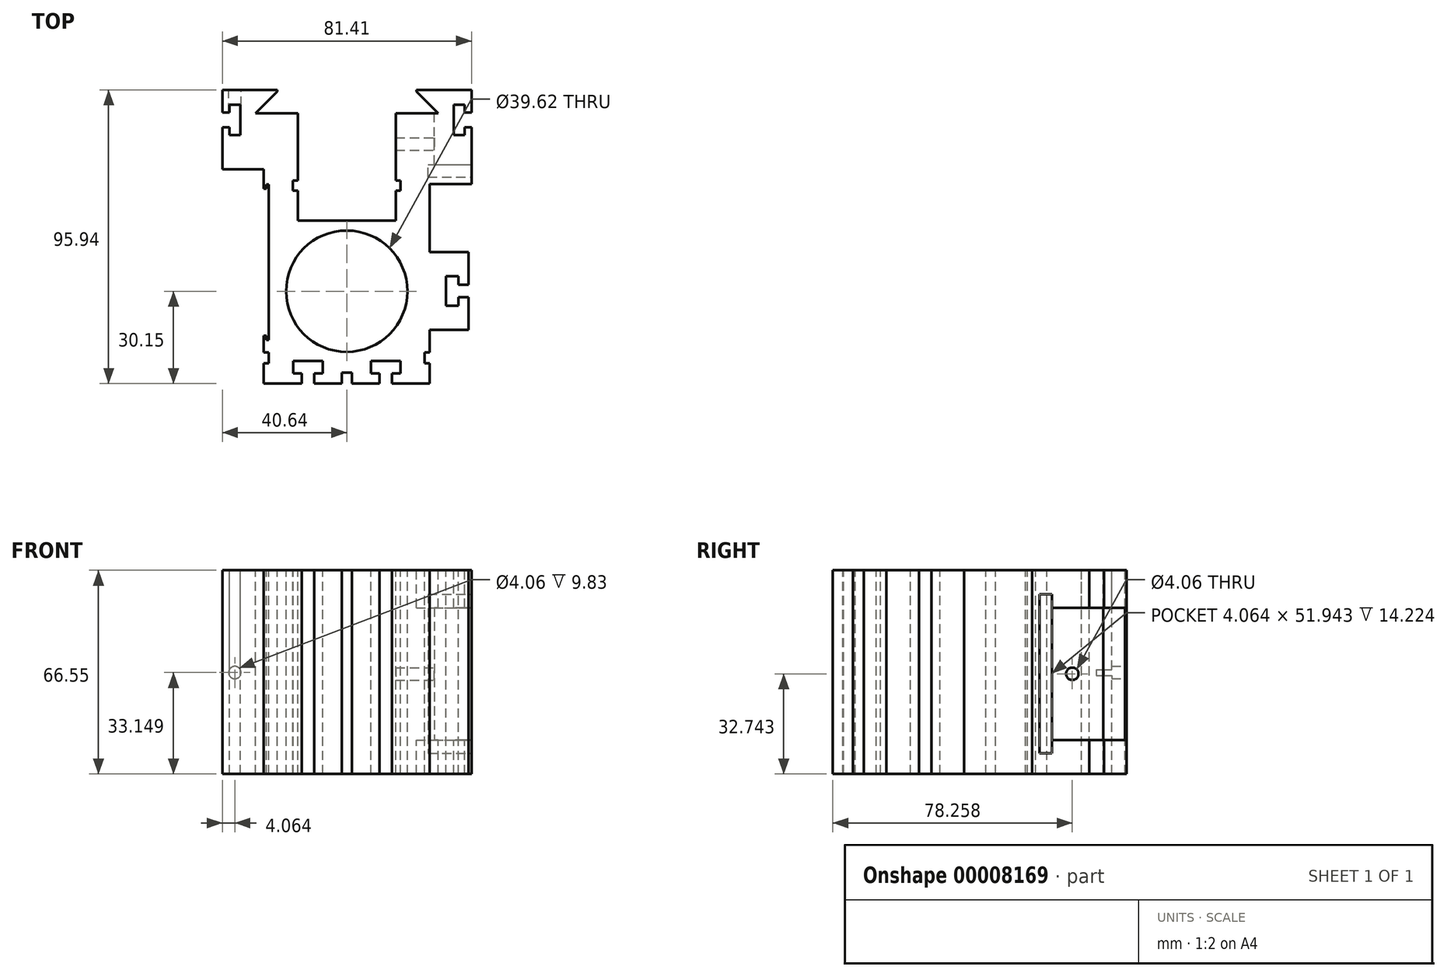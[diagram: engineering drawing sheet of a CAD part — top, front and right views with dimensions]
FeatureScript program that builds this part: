
annotation { "Feature Type Name" : "Feature", "Feature Type Description" : "" }
export const myFeature = defineFeature(function(context is Context, id is Id, definition is map)
    precondition{}
    {
        {
            var Q0;
            Q0=qCreatedBy(makeId("Top.planeOp"),FACE);
            var sketch = newSketch(context, id + "F0", { "sketchPlane" : qUnion([Q0])});
            skFitSpline(sketch, "E0.0.0", {"points": [v(-16, 23.06) * mm, v(-16, 32.87) * mm]});
            skFitSpline(sketch, "E0.0.1", {"points": [v(-16, 32.87) * mm, v(-17.6, 32.87) * mm]});
            skFitSpline(sketch, "E0.0.2", {"points": [v(-17.6, 32.87) * mm, v(-17.6, 36.17) * mm]});
            skFitSpline(sketch, "E0.0.3", {"points": [v(-17.6, 36.17) * mm, v(-16, 36.17) * mm]});
            skFitSpline(sketch, "E0.0.4", {"points": [v(-16, 36.17) * mm, v(-16, 58.17) * mm]});
            skFitSpline(sketch, "E0.0.5", {"points": [v(-16, 58.17) * mm, v(-29.84, 58.17) * mm]});
            skFitSpline(sketch, "E0.0.6", {"points": [v(-29.84, 58.17) * mm, v(-22.73, 65.28) * mm]});
            skFitSpline(sketch, "E0.0.7", {"points": [v(-22.73, 65.28) * mm, v(-22.73, 65.79) * mm]});
            skFitSpline(sketch, "E0.0.8", {"points": [v(-22.73, 65.79) * mm, v(-40.64, 65.79) * mm]});
            skFitSpline(sketch, "E0.0.9", {"points": [v(-40.64, 65.79) * mm, v(-40.64, 58.42) * mm]});
            skFitSpline(sketch, "E0.0.10", {"points": [v(-40.64, 58.42) * mm, v(-38.35, 58.42) * mm]});
            skFitSpline(sketch, "E0.0.11", {"points": [v(-38.35, 58.42) * mm, v(-38.35, 60.96) * mm]});
            skFitSpline(sketch, "E0.0.12", {"points": [v(-38.35, 60.96) * mm, v(-34.8, 60.96) * mm]});
            skFitSpline(sketch, "E0.0.13", {"points": [v(-34.8, 60.96) * mm, v(-34.8, 51.05) * mm]});
            skFitSpline(sketch, "E0.0.14", {"points": [v(-34.8, 51.05) * mm, v(-38.35, 51.05) * mm]});
            skFitSpline(sketch, "E0.0.15", {"points": [v(-38.35, 51.05) * mm, v(-38.35, 53.6) * mm]});
            skFitSpline(sketch, "E0.0.16", {"points": [v(-38.35, 53.6) * mm, v(-40.64, 53.6) * mm]});
            skFitSpline(sketch, "E0.0.17", {"points": [v(-40.64, 53.6) * mm, v(-40.64, 39.83) * mm]});
            skFitSpline(sketch, "E0.0.18", {"points": [v(-40.64, 39.83) * mm, v(-27.1, 39.83) * mm]});
            skFitSpline(sketch, "E0.0.19", {"points": [v(-27.1, 39.83) * mm, v(-27.1, 33.48) * mm]});
            skFitSpline(sketch, "E0.0.20", {"points": [v(-27.1, 33.48) * mm, v(-26.24, 33.48) * mm]});
            skFitSpline(sketch, "E0.0.21", {"points": [v(-26.24, 33.48) * mm, v(-26.24, 34.93) * mm]});
            skFitSpline(sketch, "E0.0.22", {"points": [v(-26.24, 34.93) * mm, v(-25.45, 34.93) * mm]});
            skFitSpline(sketch, "E0.0.23", {"points": [v(-25.45, 34.93) * mm, v(-25.45, -15.98) * mm]});
            skFitSpline(sketch, "E0.0.24", {"points": [v(-25.45, -15.98) * mm, v(-26.24, -15.98) * mm]});
            skFitSpline(sketch, "E0.0.25", {"points": [v(-26.24, -15.98) * mm, v(-26.24, -14.53) * mm]});
            skFitSpline(sketch, "E0.0.26", {"points": [v(-26.24, -14.53) * mm, v(-27.1, -14.53) * mm]});
            skFitSpline(sketch, "E0.0.27", {"points": [v(-27.1, -14.53) * mm, v(-27.1, -19.99) * mm]});
            skFitSpline(sketch, "E0.0.28", {"points": [v(-27.1, -19.99) * mm, v(-25.45, -19.99) * mm]});
            skFitSpline(sketch, "E0.0.29", {"points": [v(-25.45, -19.99) * mm, v(-25.45, -23.55) * mm]});
            skFitSpline(sketch, "E0.0.30", {"points": [v(-25.45, -23.55) * mm, v(-27.1, -23.55) * mm]});
            skFitSpline(sketch, "E0.0.31", {"points": [v(-27.1, -23.55) * mm, v(-27.1, -30.15) * mm]});
            skFitSpline(sketch, "E0.0.32", {"points": [v(-27.1, -30.15) * mm, v(-14.73, -30.15) * mm]});
            skFitSpline(sketch, "E0.0.33", {"points": [v(-14.73, -30.15) * mm, v(-14.73, -26.85) * mm]});
            skFitSpline(sketch, "E0.0.34", {"points": [v(-14.73, -26.85) * mm, v(-17.53, -26.85) * mm]});
            skFitSpline(sketch, "E0.0.35", {"points": [v(-17.53, -26.85) * mm, v(-17.53, -22.78) * mm]});
            skFitSpline(sketch, "E0.0.36", {"points": [v(-17.53, -22.78) * mm, v(-7.87, -22.78) * mm]});
            skFitSpline(sketch, "E0.0.37", {"points": [v(-7.87, -22.78) * mm, v(-7.87, -26.85) * mm]});
            skFitSpline(sketch, "E0.0.38", {"points": [v(-7.87, -26.85) * mm, v(-10.67, -26.85) * mm]});
            skFitSpline(sketch, "E0.0.39", {"points": [v(-10.67, -26.85) * mm, v(-10.67, -30.15) * mm]});
            skFitSpline(sketch, "E0.0.40", {"points": [v(-10.67, -30.15) * mm, v(-1.65, -30.15) * mm]});
            skFitSpline(sketch, "E0.0.41", {"points": [v(-1.65, -30.15) * mm, v(-1.65, -26.6) * mm]});
            skFitSpline(sketch, "E0.0.42", {"points": [v(-1.65, -26.6) * mm, v(1.65, -26.6) * mm]});
            skFitSpline(sketch, "E0.0.43", {"points": [v(1.65, -26.6) * mm, v(1.65, -30.15) * mm]});
            skFitSpline(sketch, "E0.0.44", {"points": [v(1.65, -30.15) * mm, v(10.67, -30.15) * mm]});
            skFitSpline(sketch, "E0.0.45", {"points": [v(10.67, -30.15) * mm, v(10.67, -26.85) * mm]});
            skFitSpline(sketch, "E0.0.46", {"points": [v(10.67, -26.85) * mm, v(7.87, -26.85) * mm]});
            skFitSpline(sketch, "E0.0.47", {"points": [v(7.87, -26.85) * mm, v(7.87, -22.78) * mm]});
            skFitSpline(sketch, "E0.0.48", {"points": [v(7.87, -22.78) * mm, v(17.53, -22.78) * mm]});
            skFitSpline(sketch, "E0.0.49", {"points": [v(17.53, -22.78) * mm, v(17.53, -26.85) * mm]});
            skFitSpline(sketch, "E0.0.50", {"points": [v(17.53, -26.85) * mm, v(14.73, -26.85) * mm]});
            skFitSpline(sketch, "E0.0.51", {"points": [v(14.73, -26.85) * mm, v(14.73, -30.15) * mm]});
            skFitSpline(sketch, "E0.0.52", {"points": [v(14.73, -30.15) * mm, v(27.1, -30.15) * mm]});
            skFitSpline(sketch, "E0.0.53", {"points": [v(27.1, -30.15) * mm, v(27.1, -23.55) * mm]});
            skFitSpline(sketch, "E0.0.54", {"points": [v(27.1, -23.55) * mm, v(25.45, -23.55) * mm]});
            skFitSpline(sketch, "E0.0.55", {"points": [v(25.45, -23.55) * mm, v(25.45, -19.99) * mm]});
            skFitSpline(sketch, "E0.0.56", {"points": [v(25.45, -19.99) * mm, v(27.1, -19.99) * mm]});
            skFitSpline(sketch, "E0.0.57", {"points": [v(27.1, -19.99) * mm, v(27.1, -12.62) * mm]});
            skFitSpline(sketch, "E0.0.58", {"points": [v(27.1, -12.62) * mm, v(39.8, -12.62) * mm]});
            skFitSpline(sketch, "E0.0.59", {"points": [v(39.8, -12.62) * mm, v(39.8, -1.96) * mm]});
            skFitSpline(sketch, "E0.0.60", {"points": [v(39.8, -1.96) * mm, v(36.5, -1.96) * mm]});
            skFitSpline(sketch, "E0.0.61", {"points": [v(36.5, -1.96) * mm, v(36.5, -4.75) * mm]});
            skFitSpline(sketch, "E0.0.62", {"points": [v(36.5, -4.75) * mm, v(32.44, -4.75) * mm]});
            skFitSpline(sketch, "E0.0.63", {"points": [v(32.44, -4.75) * mm, v(32.44, 4.9) * mm]});
            skFitSpline(sketch, "E0.0.64", {"points": [v(32.44, 4.9) * mm, v(36.5, 4.9) * mm]});
            skFitSpline(sketch, "E0.0.65", {"points": [v(36.5, 4.9) * mm, v(36.5, 2.1) * mm]});
            skFitSpline(sketch, "E0.0.66", {"points": [v(36.5, 2.1) * mm, v(39.8, 2.1) * mm]});
            skFitSpline(sketch, "E0.0.67", {"points": [v(39.8, 2.1) * mm, v(39.8, 12.78) * mm]});
            skFitSpline(sketch, "E0.0.68", {"points": [v(39.8, 12.78) * mm, v(27.1, 12.78) * mm]});
            skFitSpline(sketch, "E0.0.69", {"points": [v(27.1, 12.78) * mm, v(27.1, 35) * mm]});
            skFitSpline(sketch, "E0.0.70", {"points": [v(27.1, 35) * mm, v(40.77, 35) * mm]});
            skFitSpline(sketch, "E0.0.71", {"points": [v(40.77, 35) * mm, v(40.77, 53.6) * mm]});
            skFitSpline(sketch, "E0.0.72", {"points": [v(40.77, 53.6) * mm, v(38.48, 53.6) * mm]});
            skFitSpline(sketch, "E0.0.73", {"points": [v(38.48, 53.6) * mm, v(38.48, 51.05) * mm]});
            skFitSpline(sketch, "E0.0.74", {"points": [v(38.48, 51.05) * mm, v(34.93, 51.05) * mm]});
            skFitSpline(sketch, "E0.0.75", {"points": [v(34.93, 51.05) * mm, v(34.93, 60.96) * mm]});
            skFitSpline(sketch, "E0.0.76", {"points": [v(34.93, 60.96) * mm, v(38.48, 60.96) * mm]});
            skFitSpline(sketch, "E0.0.77", {"points": [v(38.48, 60.96) * mm, v(38.48, 58.42) * mm]});
            skFitSpline(sketch, "E0.0.78", {"points": [v(38.48, 58.42) * mm, v(40.77, 58.42) * mm]});
            skFitSpline(sketch, "E0.0.79", {"points": [v(40.77, 58.42) * mm, v(40.77, 65.79) * mm]});
            skFitSpline(sketch, "E0.0.80", {"points": [v(40.77, 65.79) * mm, v(22.73, 65.79) * mm]});
            skFitSpline(sketch, "E0.0.81", {"points": [v(22.73, 65.79) * mm, v(22.73, 65.28) * mm]});
            skFitSpline(sketch, "E0.0.82", {"points": [v(22.73, 65.28) * mm, v(29.84, 58.17) * mm]});
            skFitSpline(sketch, "E0.0.83", {"points": [v(29.84, 58.17) * mm, v(16, 58.17) * mm]});
            skFitSpline(sketch, "E0.0.84", {"points": [v(16, 58.17) * mm, v(16, 36.17) * mm]});
            skFitSpline(sketch, "E0.0.85", {"points": [v(16, 36.17) * mm, v(17.6, 36.17) * mm]});
            skFitSpline(sketch, "E0.0.86", {"points": [v(17.6, 36.17) * mm, v(17.6, 32.87) * mm]});
            skFitSpline(sketch, "E0.0.87", {"points": [v(17.6, 32.87) * mm, v(16, 32.87) * mm]});
            skFitSpline(sketch, "E0.0.88", {"points": [v(16, 32.87) * mm, v(16, 23.06) * mm]});
            skFitSpline(sketch, "E0.0.89", {"points": [v(16, 23.06) * mm, v(-16, 23.06) * mm]});
            skCircle(sketch, "E1", {"center": v(0, 0) * mm, "radius": 19.81 * mm});
            skSolve(sketch);
        }
        {
            var Q0;
            Q0=makeQuery(id+"F0.imprint","IMPRINT",FACE,{"disambiguationData":[TD([[makeQuery(id+"F0.imprint","IMPRINT",EDGE,{"derivedFrom":sQuery(id+"F0.wireOp",EDGE,"E0.0.0")}),1.0]])]});
            extrude(context, id + "F1", {"entities" : qUnion([Q0]), "oppositeDirection" : true, "depth" : 66.55 * mm});
        }
        {
            var Q0;
            Q0=makeQuery(id+"F1.opExtrude","SWEPT_FACE",FACE,{"disambiguationData":[OSD([sQuery(id+"F0.wireOp",EDGE,"E0.0.71")])]});
            var sketch = newSketch(context, id + "F2", { "sketchPlane" : qUnion([Q0])});
            skLineSegment(sketch, "E2.bottom", {"start": v(37.34, -7.77) * mm, "end": v(41.4, -7.77) * mm});
            skLineSegment(sketch, "E2.top", {"start": v(37.34, -59.72) * mm, "end": v(41.4, -59.72) * mm});
            skLineSegment(sketch, "E2.left", {"start": v(37.34, -7.77) * mm, "end": v(37.34, -59.72) * mm});
            skLineSegment(sketch, "E2.right", {"start": v(41.4, -7.77) * mm, "end": v(41.4, -59.72) * mm});
            skLineSegment(sketch, "E3", {"start": v(0, 0) * mm, "end": v(72.99, 0) * mm, "construction": true});
            skLineSegment(sketch, "E4", {"start": v(0, 0) * mm, "end": v(0, -66.55) * mm, "construction": true});
            skLineSegment(sketch, "E5", {"start": v(0, -66.55) * mm, "end": v(72.99, -66.55) * mm, "construction": true});
            skLineSegment(sketch, "E6", {"start": v(65.79, 5.15) * mm, "end": v(65.79, -75.06) * mm, "construction": true});
            skSolve(sketch);
        }
        {
            var Q0;
            Q0 = qSketchRegion(id + "F2", true);
            extrude(context, id + "F3", {"entities" : qUnion([Q0]), "operationType" : NewBodyOperationType.REMOVE, "oppositeDirection" : true, "depth" : 14.22 * mm});
        }
        {
            var Q0;
            Q0=makeQuery(id+"F1.opExtrude","SWEPT_FACE",FACE,{"disambiguationData":[OSD([sQuery(id+"F0.wireOp",EDGE,"E0.0.71")])]});
            var sketch = newSketch(context, id + "F4", { "sketchPlane" : qUnion([Q0])});
            skLineSegment(sketch, "E7", {"start": v(0, 0) * mm, "end": v(65.79, 0) * mm, "construction": true});
            skLineSegment(sketch, "E8", {"start": v(65.79, 0) * mm, "end": v(65.79, -61.54) * mm, "construction": true});
            skLineSegment(sketch, "E9.bottom", {"start": v(41.4, -12.22) * mm, "end": v(65.79, -12.22) * mm});
            skLineSegment(sketch, "E9.top", {"start": v(41.4, -55.4) * mm, "end": v(65.79, -55.4) * mm});
            skLineSegment(sketch, "E9.left", {"start": v(41.4, -12.22) * mm, "end": v(41.4, -55.4) * mm});
            skLineSegment(sketch, "E9.right", {"start": v(65.79, -12.22) * mm, "end": v(65.79, -55.4) * mm});
            skSolve(sketch);
        }
        {
            var Q0;
            Q0 = qSketchRegion(id + "F4", true);
            var Q1;
            Q1=makeQuery(id+"F1.opExtrude","SWEPT_FACE",FACE,{"disambiguationData":[OSD([sQuery(id+"F0.wireOp",EDGE,"E0.0.84")])]});
            extrude(context, id + "F5", {"entities" : qUnion([Q0]), "operationType" : NewBodyOperationType.REMOVE, "oppositeDirection" : true, "endBoundEntity" : qUnion([Q1]), "depth" : 12.2 * mm});
        }
        {
            var Q0;
            Q0=makeQuery(id+"F5.boolean.opBoolean","COPY",FACE,{"disambiguationData":[OD(0.0)],"derivedFrom":makeQuery(id+"F5.opExtrude","CAP_FACE",FACE,{"disambiguationData":[OSD([sQuery(id+"F4.wireOp",EDGE,"E9.bottom"),sQuery(id+"F4.wireOp",EDGE,"E9.top"),sQuery(id+"F4.wireOp",EDGE,"E9.left"),sQuery(id+"F4.wireOp",EDGE,"E9.right")])],"isStart":false})});
            var sketch = newSketch(context, id + "F6", { "sketchPlane" : qUnion([Q0])});
            skCircle(sketch, "E10", {"center": v(48.1, -33.8) * mm, "radius": 2.03 * mm});
            skLineSegment(sketch, "E11.bottom", {"start": v(58.17, -12.22) * mm, "end": v(65.79, -12.22) * mm});
            skLineSegment(sketch, "E11.top", {"start": v(58.17, -55.4) * mm, "end": v(65.79, -55.4) * mm});
            skLineSegment(sketch, "E11.left", {"start": v(58.17, -12.22) * mm, "end": v(58.17, -55.4) * mm});
            skLineSegment(sketch, "E11.right", {"start": v(65.79, -12.22) * mm, "end": v(65.79, -55.4) * mm});
            skSolve(sketch);
        }
        {
            var Q0;
            Q0 = qSketchRegion(id + "F6", true);
            var Q1;
            Q1=makeQuery(id+"F1.opExtrude","SWEPT_FACE",FACE,{"disambiguationData":[OSD([sQuery(id+"F0.wireOp",EDGE,"E0.0.84")])]});
            extrude(context, id + "F7", {"entities" : qUnion([Q0]), "operationType" : NewBodyOperationType.REMOVE, "endBound" : BoundingType.UP_TO_SURFACE, "oppositeDirection" : true, "endBoundEntityFace" : qUnion([Q1]), "depth" : 25.4 * mm});
        }
        {
            var Q0;
            Q0=makeQuery(id+"F1.opExtrude","SWEPT_FACE",FACE,{"disambiguationData":[OSD([sQuery(id+"F0.wireOp",EDGE,"E0.0.8")])]});
            var sketch = newSketch(context, id + "F8", { "sketchPlane" : qUnion([Q0])});
            skCircle(sketch, "E12", {"center": v(36.58, -33.4) * mm, "radius": 2.03 * mm});
            skLineSegment(sketch, "E13", {"start": v(0, -66.55) * mm, "end": v(40.64, -66.55) * mm, "construction": true});
            skSolve(sketch);
        }
        {
            var Q0;
            Q0 = qSketchRegion(id + "F8", true);
            extrude(context, id + "F9", {"entities" : qUnion([Q0]), "operationType" : NewBodyOperationType.REMOVE, "oppositeDirection" : true, "depth" : 9.83 * mm});
        }
    });
